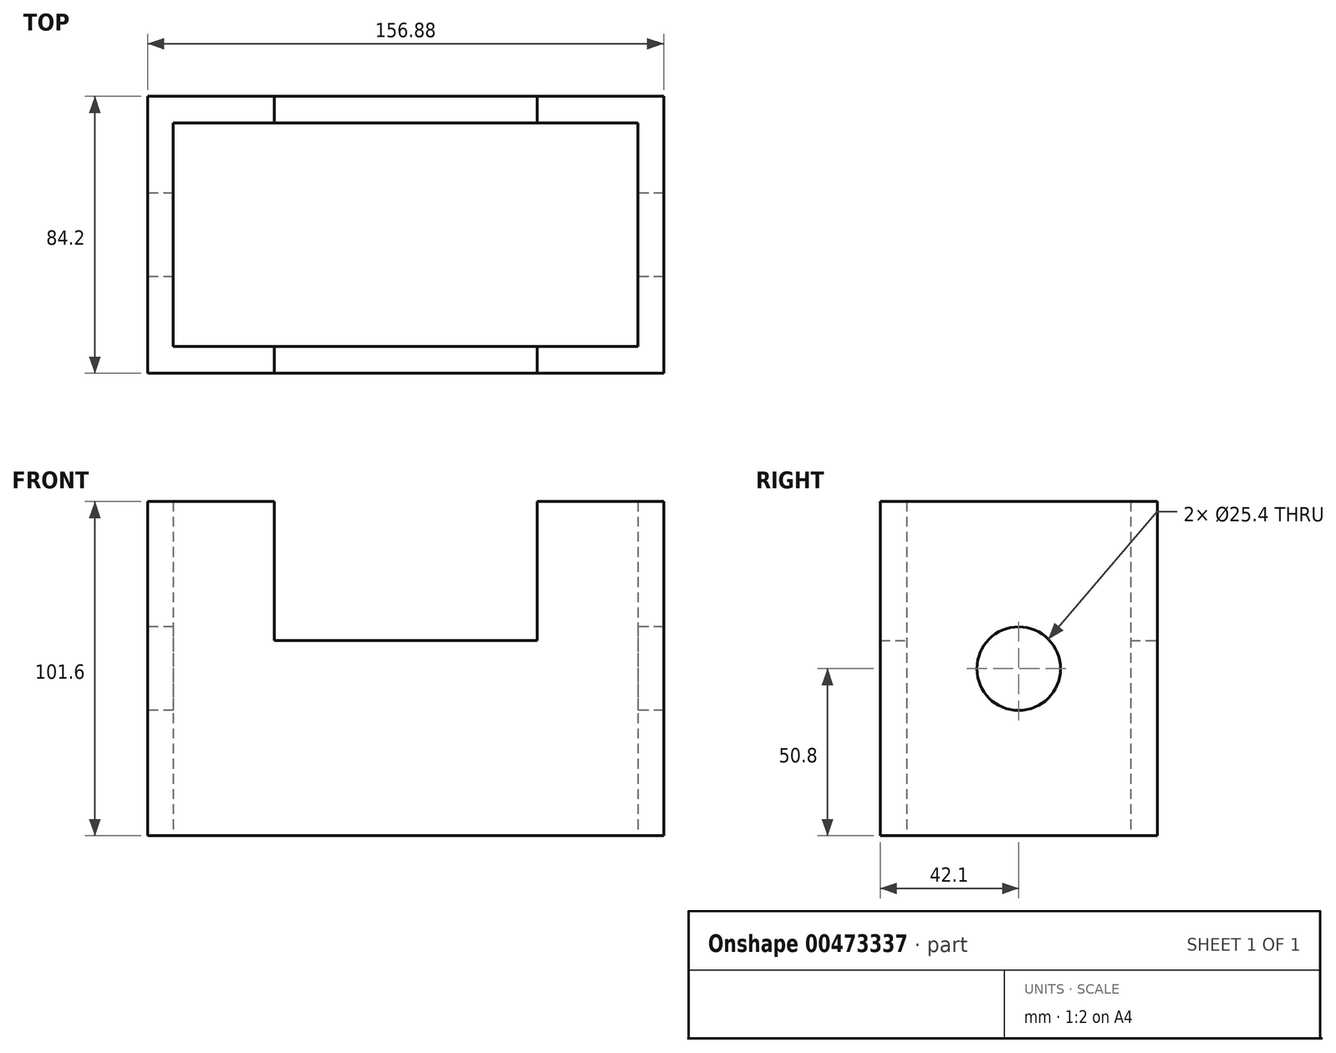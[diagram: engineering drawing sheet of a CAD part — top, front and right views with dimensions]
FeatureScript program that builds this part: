
annotation { "Feature Type Name" : "Feature", "Feature Type Description" : "" }
export const myFeature = defineFeature(function(context is Context, id is Id, definition is map)
    precondition{}
    {
        {
            var Q0;
            Q0=qCreatedBy(makeId("Top.planeOp"),FACE);
            var sketch = newSketch(context, id + "F0", { "sketchPlane" : qUnion([Q0])});
            skLineSegment(sketch, "E0.bottom", {"start": v(78.44, -42.1) * mm, "end": v(-78.44, -42.1) * mm});
            skLineSegment(sketch, "E0.top", {"start": v(78.44, 42.1) * mm, "end": v(-78.44, 42.1) * mm});
            skLineSegment(sketch, "E0.left", {"start": v(78.44, -42.1) * mm, "end": v(78.44, 42.1) * mm});
            skLineSegment(sketch, "E0.right", {"start": v(-78.44, -42.1) * mm, "end": v(-78.44, 42.1) * mm});
            skPoint(sketch, "E0.middle", {"position": v(0, 0) * mm});
            skLineSegment(sketch, "E1.bottom", {"start": v(70.6, -34) * mm, "end": v(-70.6, -34) * mm});
            skLineSegment(sketch, "E1.top", {"start": v(70.6, 34) * mm, "end": v(-70.6, 34) * mm});
            skLineSegment(sketch, "E1.left", {"start": v(70.6, -34) * mm, "end": v(70.6, 34) * mm});
            skLineSegment(sketch, "E1.right", {"start": v(-70.6, -34) * mm, "end": v(-70.6, 34) * mm});
            skSolve(sketch);
        }
        {
            var Q0;
            Q0=makeQuery(id+"F0.imprint","IMPRINT",FACE,{"disambiguationData":[TD([[makeQuery(id+"F0.imprint","IMPRINT",EDGE,{"derivedFrom":sQuery(id+"F0.wireOp",EDGE,"E0.bottom")}),-1.0]])]});
            extrude(context, id + "F1", {"entities" : qUnion([Q0]), "depth" : 101.6 * mm});
        }
        {
            var Q0;
            Q0=makeQuery(id+"F1.opExtrude","SWEPT_FACE",FACE,{"disambiguationData":[OSD([sQuery(id+"F0.wireOp",EDGE,"E0.bottom")])]});
            var sketch = newSketch(context, id + "F2", { "sketchPlane" : qUnion([Q0])});
            skLineSegment(sketch, "E2.bottom", {"start": v(39.96, 59.37) * mm, "end": v(-39.96, 59.37) * mm});
            skLineSegment(sketch, "E2.top", {"start": v(39.96, 143.83) * mm, "end": v(-39.96, 143.83) * mm});
            skLineSegment(sketch, "E2.left", {"start": v(39.96, 59.37) * mm, "end": v(39.96, 143.83) * mm});
            skLineSegment(sketch, "E2.right", {"start": v(-39.96, 59.37) * mm, "end": v(-39.96, 143.83) * mm});
            skPoint(sketch, "E2.middle", {"position": v(0, 101.6) * mm});
            skSolve(sketch);
        }
        {
            var Q0;
            {var subQ0=sQuery(id+"F2.wireOp",EDGE,"E2.bottom");Q0=makeQuery(id+"F2.imprint","IMPRINT",FACE,{"disambiguationData":[TD([[makeQuery(id+"F2.imprint","IMPRINT",EDGE,{"derivedFrom":subQ0}),-1.0]])]});}
            extrude(context, id + "F3", {"entities" : qUnion([Q0]), "operationType" : NewBodyOperationType.REMOVE, "endBound" : BoundingType.SYMMETRIC, "depth" : 381.5 * mm});
        }
        {
            var Q0;
            Q0=makeQuery(id+"F1.opExtrude","SWEPT_FACE",FACE,{"disambiguationData":[OSD([sQuery(id+"F0.wireOp",EDGE,"E0.right")])]});
            var sketch = newSketch(context, id + "F4", { "sketchPlane" : qUnion([Q0])});
            skLineSegment(sketch, "E3", {"start": v(0, 0) * mm, "end": v(0, 101.6) * mm});
            skPoint(sketch, "E4", {"position": v(0, 50.8) * mm});
            skSolve(sketch);
        }
        {
            var Q0;
            Q0=sQuery(id+"F4.wireOp",VERTEX,"E4");
            var Q1;
            Q1=makeQuery(id+"F1.opExtrude","SWEPT_BODY",BODY,{"disambiguationData":[OSD([sQuery(id+"F0.wireOp",EDGE,"E0.bottom"),sQuery(id+"F0.wireOp",EDGE,"E0.top"),sQuery(id+"F0.wireOp",EDGE,"E0.left"),sQuery(id+"F0.wireOp",EDGE,"E0.right"),sQuery(id+"F0.wireOp",EDGE,"E1.bottom"),sQuery(id+"F0.wireOp",EDGE,"E1.top"),sQuery(id+"F0.wireOp",EDGE,"E1.left"),sQuery(id+"F0.wireOp",EDGE,"E1.right")])]});
            hole(context, id + "F5", {"style" : HoleStyle.SIMPLE, "endStyle" : HoleEndStyle.THROUGH, "holeDiameter" : 25.4 * mm, "isTappedThrough" : true, "tappedDepth" : 12.7 * mm, "tapClearance" : 3, "locations" : qUnion([Q0]), "scope" : qUnion([Q1])});
        }
    });
